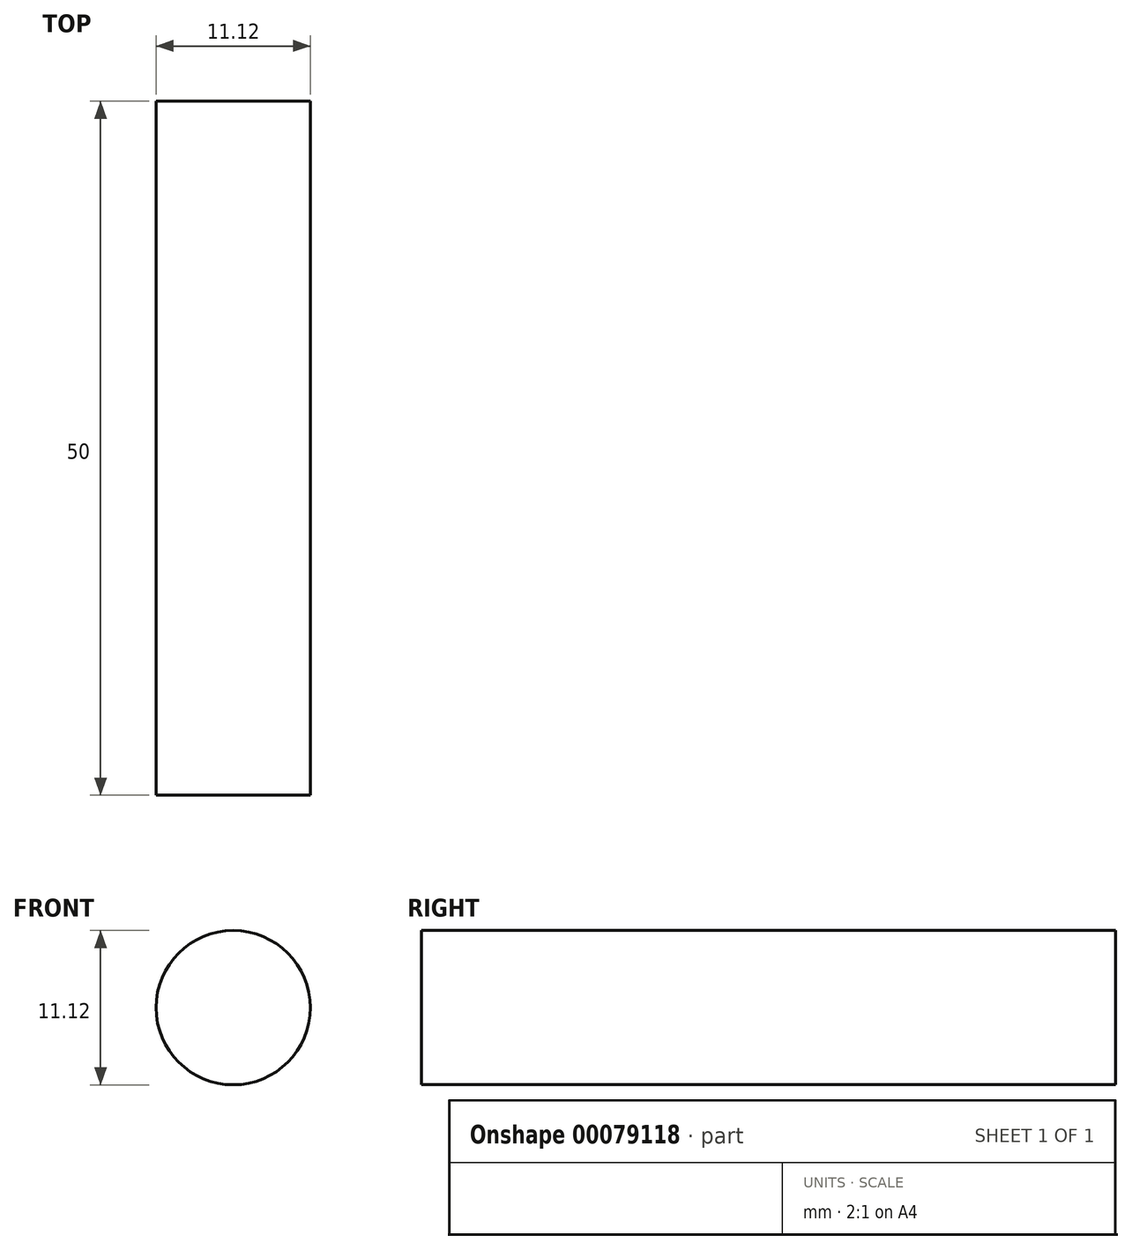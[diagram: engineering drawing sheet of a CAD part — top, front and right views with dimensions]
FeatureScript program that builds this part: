
annotation { "Feature Type Name" : "Feature", "Feature Type Description" : "" }
export const myFeature = defineFeature(function(context is Context, id is Id, definition is map)
    precondition{}
    {
        {
            var Q0;
            Q0=qCreatedBy(makeId("Front.planeOp"),FACE);
            var sketch = newSketch(context, id + "F0", { "sketchPlane" : qUnion([Q0])});
            skCircle(sketch, "E0", {"center": v(0, 0) * mm, "radius": 5.56 * mm});
            skSolve(sketch);
        }
        {
            var Q0;
            Q0 = qSketchRegion(id + "F0", true);
            extrude(context, id + "F1", {"entities" : qUnion([Q0]), "depth" : 50 * mm});
        }
    });
